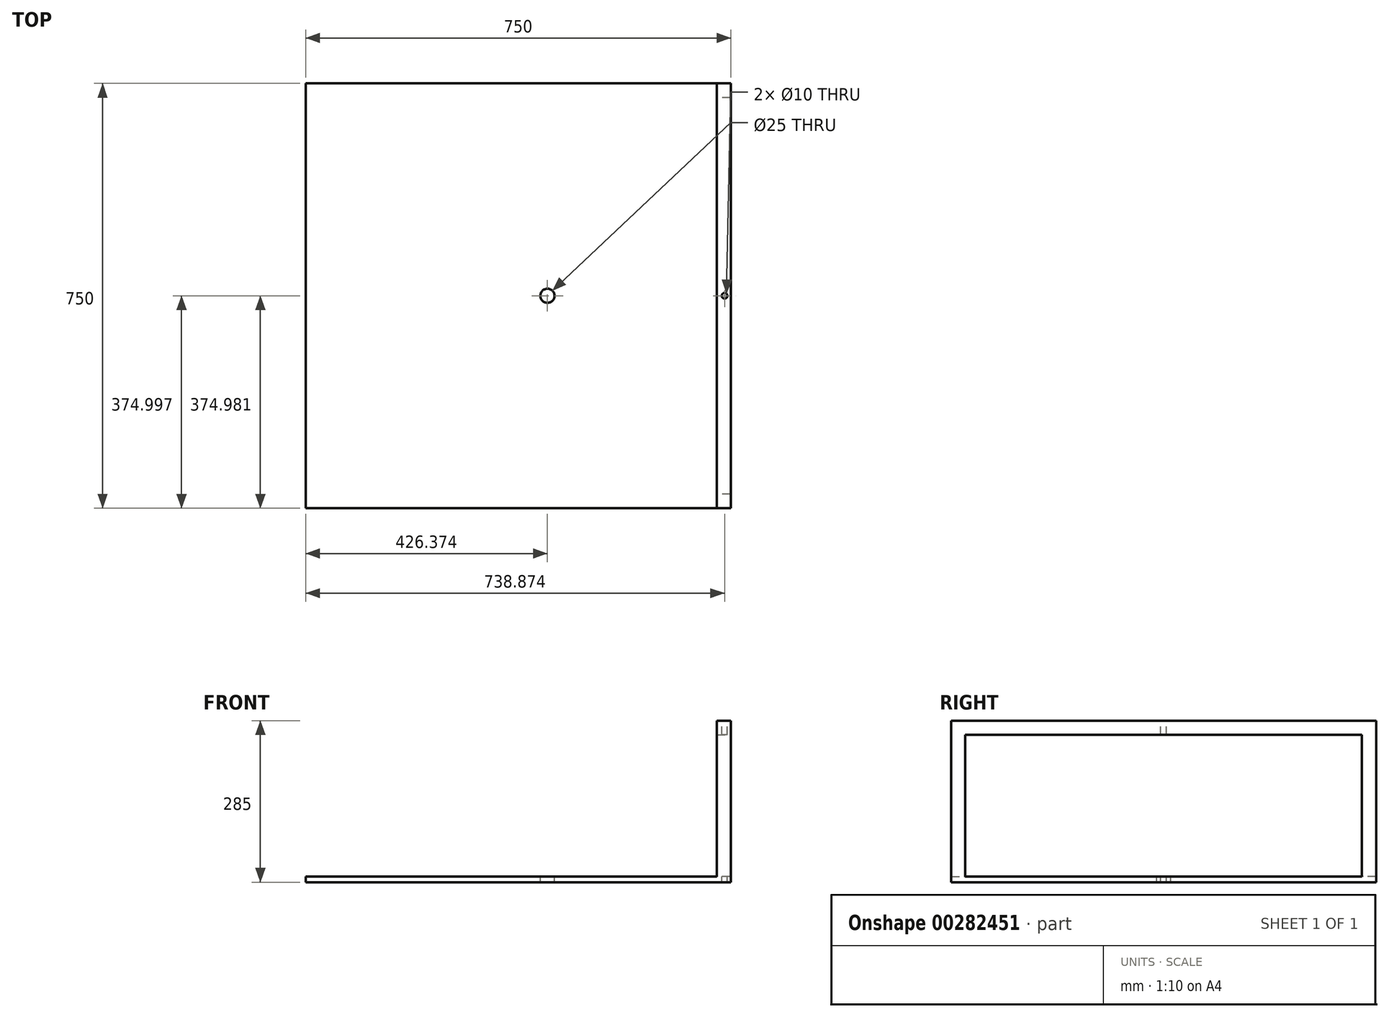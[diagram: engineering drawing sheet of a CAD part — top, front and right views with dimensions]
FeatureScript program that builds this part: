
annotation { "Feature Type Name" : "Feature", "Feature Type Description" : "" }
export const myFeature = defineFeature(function(context is Context, id is Id, definition is map)
    precondition{}
    {
        {
            var Q0;
            Q0=qCreatedBy(makeId("Top.planeOp"),FACE);
            var sketch = newSketch(context, id + "F0", { "sketchPlane" : qUnion([Q0])});
            skLineSegment(sketch, "E0.bottom", {"start": v(-840.58, 705.5) * mm, "end": v(-90.58, 705.5) * mm});
            skLineSegment(sketch, "E0.top", {"start": v(-840.58, -44.5) * mm, "end": v(-90.58, -44.5) * mm});
            skLineSegment(sketch, "E0.left", {"start": v(-840.58, 705.5) * mm, "end": v(-840.58, -44.5) * mm});
            skLineSegment(sketch, "E0.right", {"start": v(-90.58, 705.5) * mm, "end": v(-90.58, -44.5) * mm});
            skSolve(sketch);
        }
        {
            var Q0;
            Q0=makeQuery(id+"F0.imprint","IMPRINT",FACE,{"disambiguationData":[TD([[makeQuery(id+"F0.imprint","IMPRINT",EDGE,{"derivedFrom":sQuery(id+"F0.wireOp",EDGE,"E0.bottom")}),-1.0]])]});
            extrude(context, id + "F1", {"entities" : qUnion([Q0]), "depth" : 10 * mm});
        }
        {
            var Q0;
            Q0=makeQuery(id+"F1.opExtrude","CAP_FACE",FACE,{"disambiguationData":[OSD([sQuery(id+"F0.wireOp",EDGE,"E0.bottom"),sQuery(id+"F0.wireOp",EDGE,"E0.top"),sQuery(id+"F0.wireOp",EDGE,"E0.left"),sQuery(id+"F0.wireOp",EDGE,"E0.right")])],"isStart":false});
            var sketch = newSketch(context, id + "F2", { "sketchPlane" : qUnion([Q0])});
            skLineSegment(sketch, "E1.bottom", {"start": v(-90.58, 705.5) * mm, "end": v(-115.58, 705.5) * mm});
            skLineSegment(sketch, "E1.top", {"start": v(-90.58, 680.5) * mm, "end": v(-115.58, 680.5) * mm});
            skLineSegment(sketch, "E1.left", {"start": v(-90.58, 705.5) * mm, "end": v(-90.58, 680.5) * mm});
            skLineSegment(sketch, "E1.right", {"start": v(-115.58, 705.5) * mm, "end": v(-115.58, 680.5) * mm});
            skLineSegment(sketch, "E2.bottom", {"start": v(-90.58, -44.5) * mm, "end": v(-115.58, -44.5) * mm});
            skLineSegment(sketch, "E2.top", {"start": v(-90.58, -19.5) * mm, "end": v(-115.58, -19.5) * mm});
            skLineSegment(sketch, "E2.left", {"start": v(-90.58, -44.5) * mm, "end": v(-90.58, -19.5) * mm});
            skLineSegment(sketch, "E2.right", {"start": v(-115.58, -44.5) * mm, "end": v(-115.58, -19.5) * mm});
            skSolve(sketch);
        }
        {
            var Q0;
            Q0=makeQuery(id+"F2.imprint","IMPRINT",FACE,{"disambiguationData":[TD([[makeQuery(id+"F2.imprint","IMPRINT",EDGE,{"derivedFrom":sQuery(id+"F2.wireOp",EDGE,"E2.bottom")}),1.0]])]});
            var Q1;
            Q1=makeQuery(id+"F2.imprint","IMPRINT",FACE,{"disambiguationData":[TD([[makeQuery(id+"F2.imprint","IMPRINT",EDGE,{"derivedFrom":sQuery(id+"F2.wireOp",EDGE,"E1.bottom")}),-1.0]])]});
            extrude(context, id + "F3", {"entities" : qUnion([Q0, Q1]), "operationType" : NewBodyOperationType.ADD, "depth" : 250 * mm});
        }
        {
            var Q0;
            Q0=makeQuery(id+"F3.opExtrude","CAP_FACE",FACE,{"disambiguationData":[OSD([sQuery(id+"F2.wireOp",EDGE,"E2.bottom"),sQuery(id+"F2.wireOp",EDGE,"E2.top"),sQuery(id+"F2.wireOp",EDGE,"E2.left"),sQuery(id+"F2.wireOp",EDGE,"E2.right")])],"isStart":false});
            var sketch = newSketch(context, id + "F4", { "sketchPlane" : qUnion([Q0])});
            skLineSegment(sketch, "E3.bottom", {"start": v(-90.58, -44.5) * mm, "end": v(-115.58, -44.5) * mm});
            skLineSegment(sketch, "E3.top", {"start": v(-90.58, 705.47) * mm, "end": v(-115.58, 705.47) * mm});
            skLineSegment(sketch, "E3.left", {"start": v(-90.58, -44.5) * mm, "end": v(-90.58, 705.47) * mm});
            skLineSegment(sketch, "E3.right", {"start": v(-115.58, -44.5) * mm, "end": v(-115.58, 705.47) * mm});
            skSolve(sketch);
        }
        {
            var Q0;
            Q0 = qSketchRegion(id + "F4", true);
            extrude(context, id + "F5", {"entities" : qUnion([Q0]), "operationType" : NewBodyOperationType.ADD, "depth" : 25 * mm});
        }
        {
            var Q0;
            Q0=makeQuery(id+"F5.opExtrude","CAP_FACE",FACE,{"disambiguationData":[OSD([sQuery(id+"F4.wireOp",EDGE,"E3.bottom"),sQuery(id+"F4.wireOp",EDGE,"E3.top"),sQuery(id+"F4.wireOp",EDGE,"E3.left"),sQuery(id+"F4.wireOp",EDGE,"E3.right")])],"isStart":false});
            var sketch = newSketch(context, id + "F6", { "sketchPlane" : qUnion([Q0])});
            skCircle(sketch, "E4", {"center": v(-101.7, 330.5) * mm, "radius": 5 * mm});
            skPoint(sketch, "E4.centerSnap0", {"position": v(-90.58, 330.5) * mm});
            skSolve(sketch);
        }
        {
            var Q0;
            Q0=makeQuery(id+"F6.imprint","IMPRINT",FACE,{"disambiguationData":[TD([[makeQuery(id+"F6.imprint","IMPRINT",EDGE,{"derivedFrom":sQuery(id+"F6.wireOp",EDGE,"E4")}),1.0]])]});
            extrude(context, id + "F7", {"entities" : qUnion([Q0]), "operationType" : NewBodyOperationType.REMOVE, "endBound" : BoundingType.THROUGH_ALL, "oppositeDirection" : true, "depth" : 25 * mm});
        }
        {
            var Q0;
            Q0=makeQuery(id+"F1.opExtrude","CAP_FACE",FACE,{"disambiguationData":[OSD([sQuery(id+"F0.wireOp",EDGE,"E0.bottom"),sQuery(id+"F0.wireOp",EDGE,"E0.top"),sQuery(id+"F0.wireOp",EDGE,"E0.left"),sQuery(id+"F0.wireOp",EDGE,"E0.right")])],"isStart":false});
            var sketch = newSketch(context, id + "F8", { "sketchPlane" : qUnion([Q0])});
            skCircle(sketch, "E5", {"center": v(-414.2, 330.5) * mm, "radius": 12.5 * mm});
            skSolve(sketch);
        }
        {
            var Q0;
            Q0=makeQuery(id+"F8.imprint","IMPRINT",FACE,{"disambiguationData":[TD([[makeQuery(id+"F8.imprint","IMPRINT",EDGE,{"derivedFrom":sQuery(id+"F8.wireOp",EDGE,"E5")}),1.0]])]});
            extrude(context, id + "F9", {"entities" : qUnion([Q0]), "operationType" : NewBodyOperationType.REMOVE, "oppositeDirection" : true, "depth" : 25 * mm});
        }
    });
